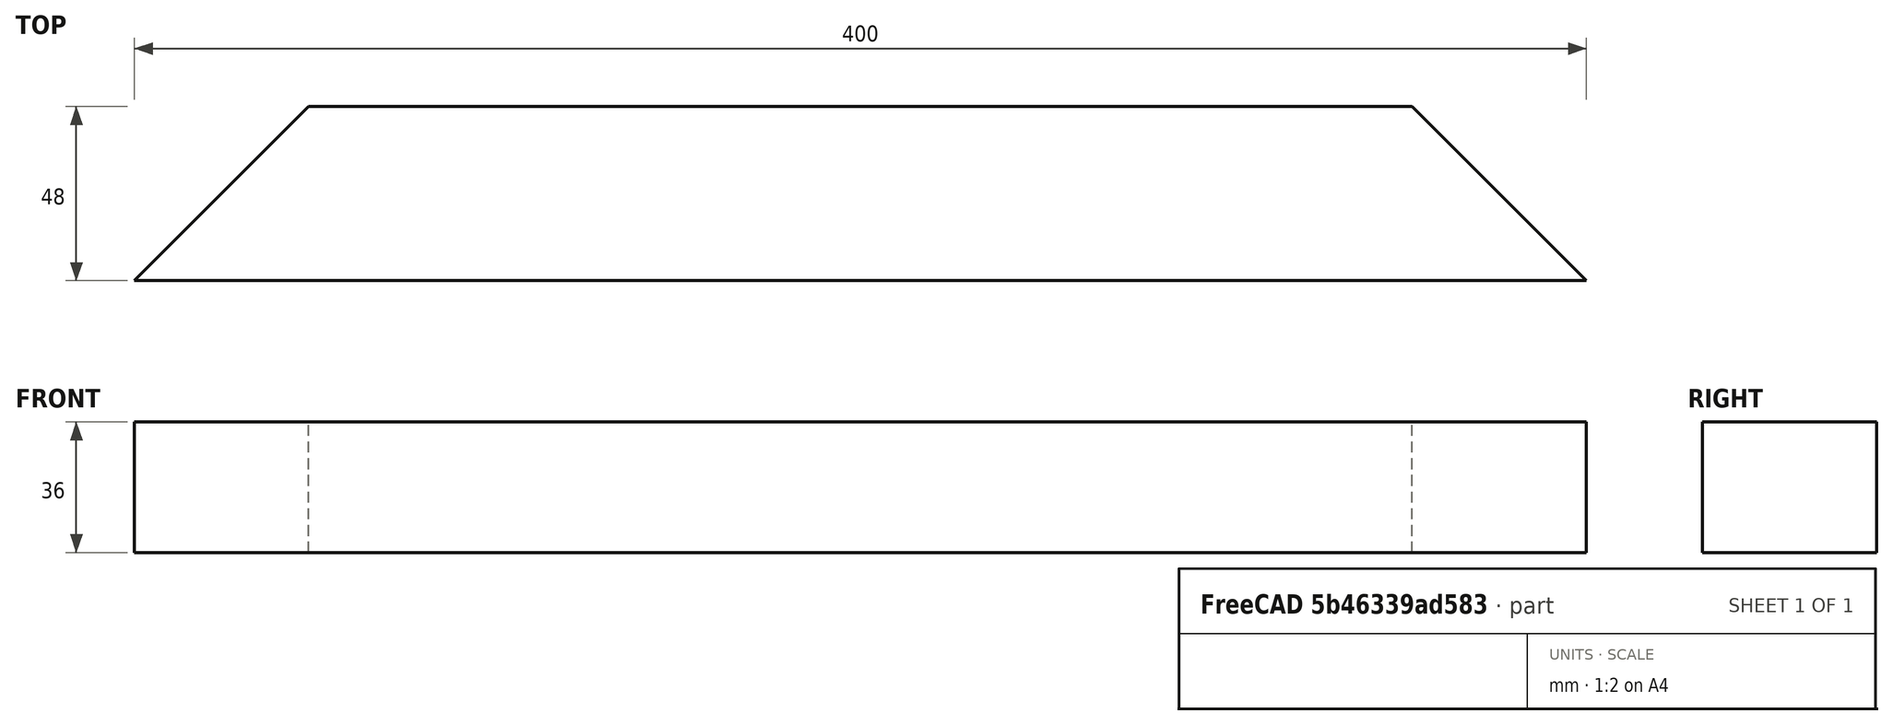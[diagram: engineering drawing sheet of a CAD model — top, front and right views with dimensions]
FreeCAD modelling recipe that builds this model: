
FCSTD DOCUMENT  (FreeCAD 0.19R24267 (Git))
Label: backTorque
License: Creative Commons Attribution-ShareAlike
LicenseURL: http://creativecommons.org/licenses/by-sa/4.0/
objects: Sketcher::SketchObject×1, Part::Extrusion×1
note: 2 computed .brp shape members not serialized (recipe doc carries the construction recipe); baked Part::Feature solids carry a one-line shape summary decoded from their .brp
EXTERNAL_REF file=Main.FCStd obj=Spreadsheet

FEATURE [Sketcher::SketchObject] Sketch
  FullyConstrained = true
  expr: Constraints[9] = Main#<<params>>.outerDeep
  expr: Constraints[8] = Main#<<params>>.structuralWoodWidth
  sketch-geometry (4):
    g0: LineSegment StartX=0 StartY=0 StartZ=0 EndX=48 EndY=48 EndZ=0
    g1: LineSegment StartX=48 StartY=48 StartZ=0 EndX=352 EndY=48 EndZ=0
    g2: LineSegment StartX=352 StartY=48 StartZ=0 EndX=400 EndY=0 EndZ=0
    g3: LineSegment StartX=400 StartY=0 StartZ=0 EndX=0 EndY=0 EndZ=0
  constraints (11):
    c: Coincident(g-1,g0)
    c: Coincident(g0,g1)
    c: Horizontal(g1)
    c: Coincident(g1,g2)
    c: PointOnObject(g2,g-1)
    c: Coincident(g2,g3)
    c: Coincident(g3,g0)
    c: Angle(g3,g0) = 0.785398
    c: DistanceY(g0,g0) = 48
    c: Distance(g3) = 400
    c: Equal(g0,g2)
FEATURE [Part::Extrusion] Extrude
  Base = -> Sketch
  Dir = (0,0,1)
  DirMode = 2
  FaceMakerClass = Part::FaceMakerBullseye
  LengthFwd = 36
  LengthRev = 0
  Solid = true
  Symmetric = false
  expr: LengthFwd = Main#<<params>>.structuralWoodHeight
